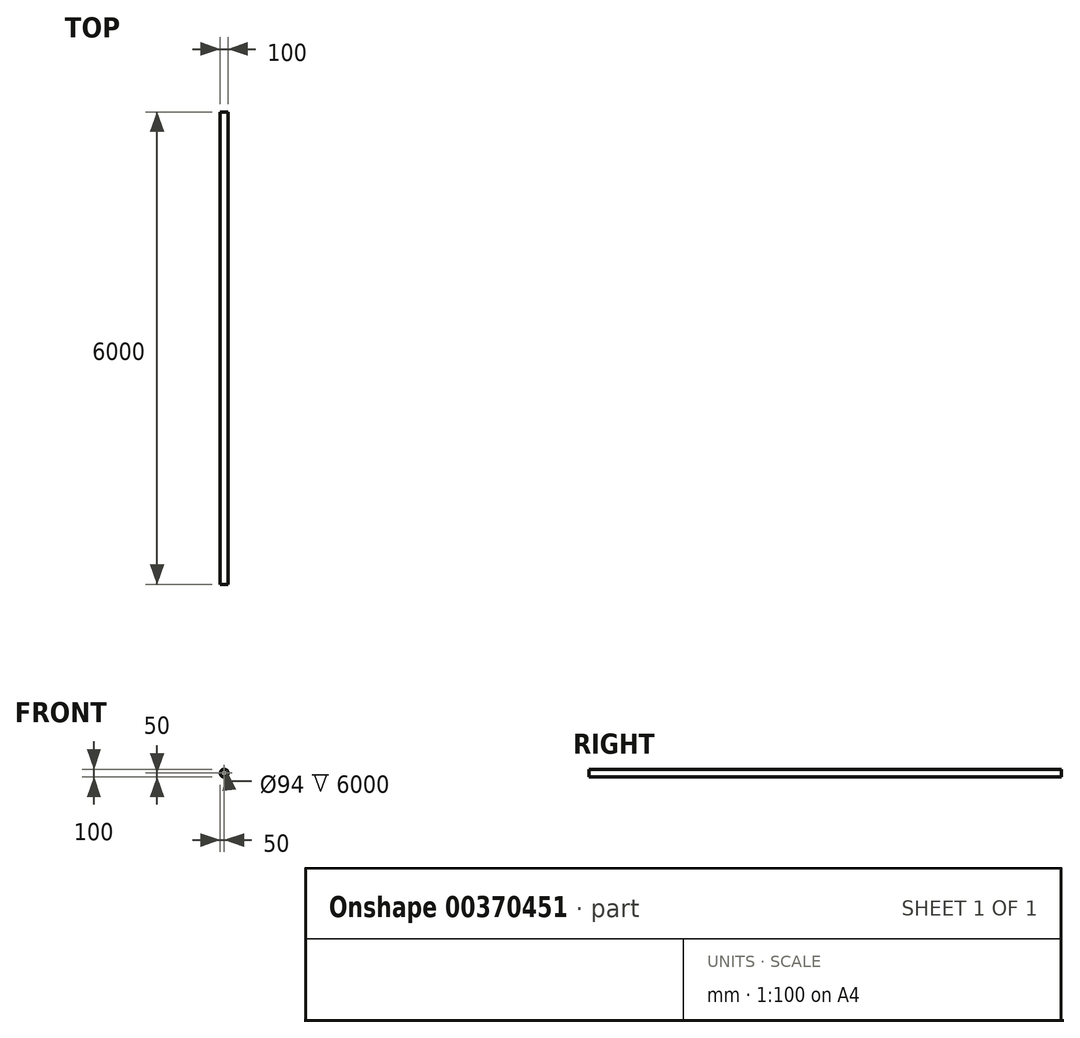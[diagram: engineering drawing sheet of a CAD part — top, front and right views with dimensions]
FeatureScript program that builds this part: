
annotation { "Feature Type Name" : "Feature", "Feature Type Description" : "" }
export const myFeature = defineFeature(function(context is Context, id is Id, definition is map)
    precondition{}
    {
        {
            var Q0;
            Q0=qCreatedBy(makeId("Front.planeOp"),FACE);
            var sketch = newSketch(context, id + "F0", { "sketchPlane" : qUnion([Q0])});
            skCircle(sketch, "E0", {"center": v(0, 0) * mm, "radius": 50 * mm});
            skCircle(sketch, "E1", {"center": v(0, 0) * mm, "radius": 47 * mm});
            skSolve(sketch);
        }
        {
            var Q0;
            Q0 = qSketchRegion(id + "F0", true);
            extrude(context, id + "F1", {"entities" : qUnion([Q0]), "depth" : 6000 * mm});
        }
    });
